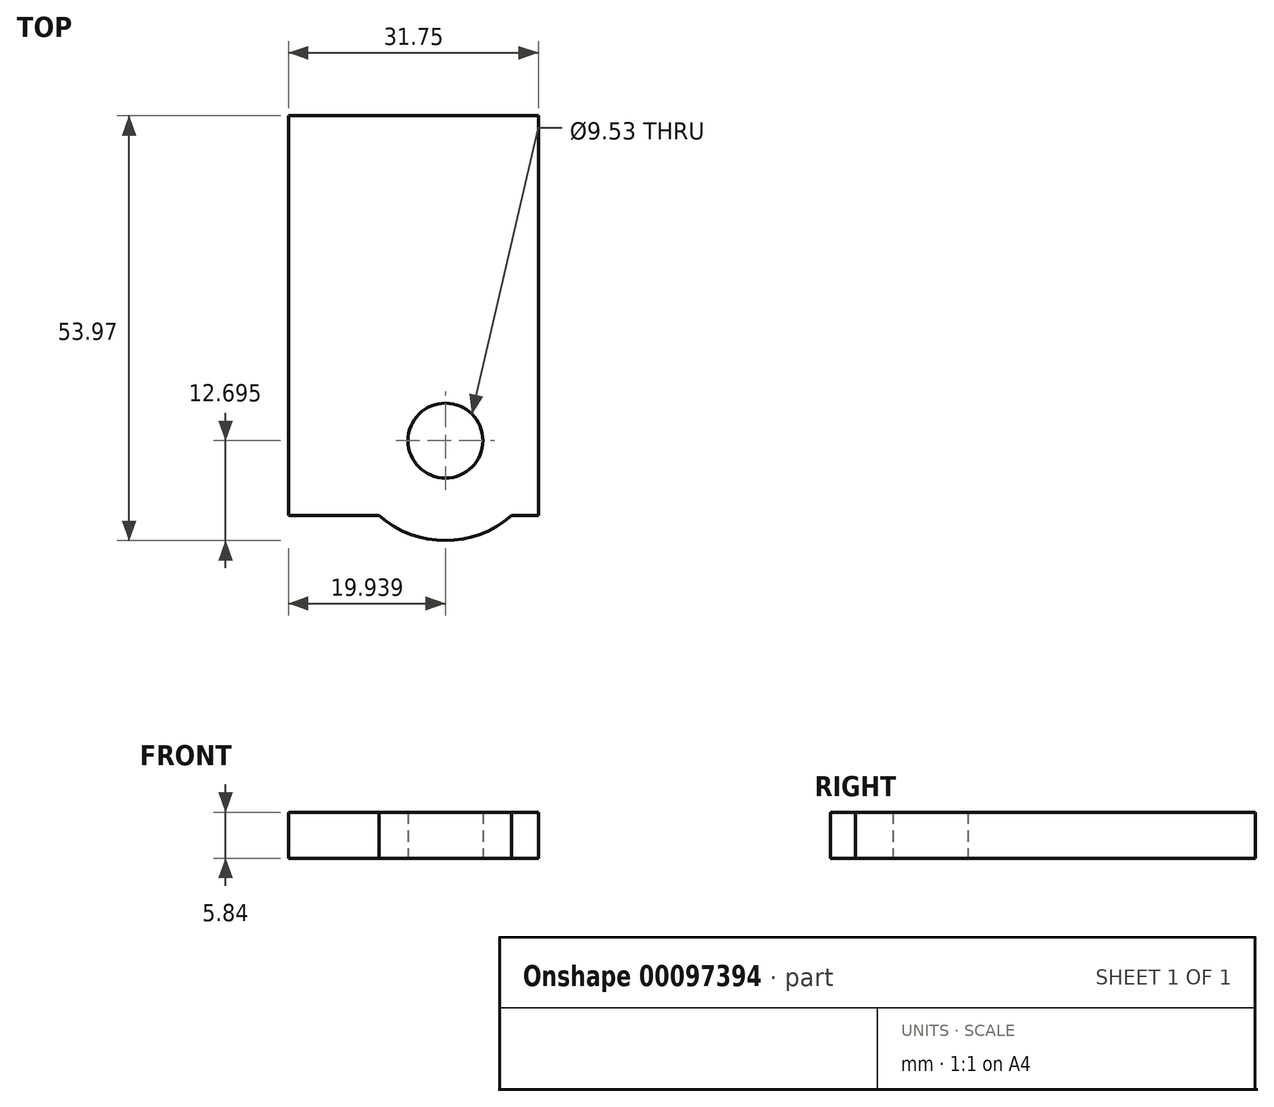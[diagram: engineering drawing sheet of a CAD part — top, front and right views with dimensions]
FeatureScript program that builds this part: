
annotation { "Feature Type Name" : "Feature", "Feature Type Description" : "" }
export const myFeature = defineFeature(function(context is Context, id is Id, definition is map)
    precondition{}
    {
        {
            var Q0;
            Q0=qCreatedBy(makeId("Top.planeOp"),FACE);
            var sketch = newSketch(context, id + "F0", { "sketchPlane" : qUnion([Q0])});
            skLineSegment(sketch, "E0.bottom", {"start": v(0, 0) * mm, "end": v(-31.75, 0) * mm});
            skLineSegment(sketch, "E0.top", {"start": v(0, 50.8) * mm, "end": v(-31.75, 50.8) * mm});
            skLineSegment(sketch, "E0.left", {"start": v(0, 0) * mm, "end": v(0, 50.8) * mm});
            skLineSegment(sketch, "E0.right", {"start": v(-31.75, 0) * mm, "end": v(-31.75, 50.8) * mm});
            skCircle(sketch, "E1", {"center": v(-11.81, 9.52) * mm, "radius": 12.7 * mm});
            skCircle(sketch, "E2", {"center": v(-11.81, 9.52) * mm, "radius": 4.76 * mm});
            skSolve(sketch);
        }
        {
            var Q0;
            Q0=makeQuery(id+"F0.imprint","IMPRINT",FACE,{"disambiguationData":[TD([[makeQuery(id+"F0.imprint","IMPRINT",EDGE,{"derivedFrom":sQuery(id+"F0.wireOp",EDGE,"E0.bottom")}),-1.0]])]});
            var Q1;
            {var subQ0=sQuery(id+"F0.wireOp",EDGE,"E0.right");var subQ1=sQuery(id+"F0.wireOp",EDGE,"E0.top");var subQ2=makeQuery(id+"F0.imprint","INTERSECT",VERTEX,{"derivedFrom":[subQ1,subQ0]});Q1=makeQuery(id+"F0.imprint","IMPRINT",FACE,{"disambiguationData":[TD([[makeQuery(id+"F0.imprint","IMPRINT",EDGE,{"disambiguationData":[TD([[subQ2,1.0]])],"derivedFrom":subQ1}),1.0]])]});}
            var Q2;
            {var subQ0=sQuery(id+"F0.wireOp",EDGE,"E0.right");var subQ1=sQuery(id+"F0.wireOp",EDGE,"E0.top");var subQ2=makeQuery(id+"F0.imprint","INTERSECT",VERTEX,{"derivedFrom":[subQ1,subQ0]});Q2=makeQuery(id+"F0.imprint","IMPRINT",FACE,{"disambiguationData":[TD([[makeQuery(id+"F0.imprint","IMPRINT",EDGE,{"disambiguationData":[TD([[subQ2,1.0]])],"derivedFrom":subQ1}),-1.0]])]});}
            var Q3;
            {var subQ0=sQuery(id+"F0.wireOp",EDGE,"E0.left");var subQ1=sQuery(id+"F0.wireOp",EDGE,"E0.bottom");var subQ2=makeQuery(id+"F0.imprint","INTERSECT",VERTEX,{"derivedFrom":[subQ1,subQ0]});Q3=makeQuery(id+"F0.imprint","IMPRINT",FACE,{"disambiguationData":[TD([[makeQuery(id+"F0.imprint","IMPRINT",EDGE,{"disambiguationData":[TD([[subQ2,-1.0]])],"derivedFrom":subQ1}),1.0]])]});}
            var Q4;
            Q4=makeQuery(id+"F0.imprint","IMPRINT",FACE,{"disambiguationData":[TD([[makeQuery(id+"F0.imprint","IMPRINT",EDGE,{"derivedFrom":sQuery(id+"F0.wireOp",EDGE,"E2")}),-1.0]])]});
            var Q5;
            {var subQ0=sQuery(id+"F0.wireOp",EDGE,"E1");var subQ1=sQuery(id+"F0.wireOp",EDGE,"E0.bottom");var subQ2=makeQuery(id+"F0.imprint","INTERSECT",VERTEX,{"disambiguationData":[OD(0.0)],"derivedFrom":[subQ1,subQ0]});Q5=makeQuery(id+"F0.imprint","IMPRINT",FACE,{"disambiguationData":[TD([[makeQuery(id+"F0.imprint","IMPRINT",EDGE,{"disambiguationData":[TD([[subQ2,-1.0]])],"derivedFrom":subQ1}),1.0]])]});}
            var Q6;
            {var subQ0=sQuery(id+"F0.wireOp",EDGE,"E1");var subQ1=sQuery(id+"F0.wireOp",EDGE,"E0.left");var subQ2=makeQuery(id+"F0.imprint","INTERSECT",VERTEX,{"disambiguationData":[OD(0.0)],"derivedFrom":[subQ1,subQ0]});Q6=makeQuery(id+"F0.imprint","IMPRINT",FACE,{"disambiguationData":[TD([[makeQuery(id+"F0.imprint","IMPRINT",EDGE,{"disambiguationData":[TD([[subQ2,-1.0]])],"derivedFrom":subQ1}),-1.0]])]});}
            extrude(context, id + "F1", {"entities" : qUnion([Q0, Q1, Q2, Q3, Q4, Q5, Q6]), "depth" : 5.84 * mm});
        }
    });
